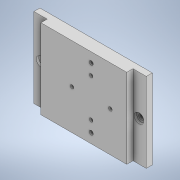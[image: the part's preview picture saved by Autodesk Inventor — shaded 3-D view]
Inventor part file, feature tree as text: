
AUTODESK INVENTOR PART (.ipt)
format: ipt  version: 2020 (Build 240168000, 168)  size: 148,480 bytes
history: native  units: in
note: dims shown in document units (in); Inventor stores cm internally (conversion verified against a paired STEP export)
features: sketch x5, hole x3, extrude x2
ambient origin geometry x8: Origin, YZ Plane, XZ Plane, XY Plane, X Axis, Y Axis, Z Axis, Center Point
bodies: Solid1 (feature_tree)
feature tree (10):
  extrude  "Extrusion1"  Depth=3.6654in
  extrude  "Extrusion2"  Depth=0.1969in TaperAngle=0.0deg
  hole  "Hole1"  [1 undecoded]
  hole  "Hole2"  [1 undecoded]
  hole  "Hole3"  [1 undecoded]
  sketch  "Sketch1"  dims[d2=0.4in d3=0.0in d4=3.6654in]
  sketch  "Sketch2"  dims[d5=2.5984in d6=0.1969in d7=0.0in]
  sketch  "Sketch3"  dims[d8=0.2362in d9=0.2362in]
  sketch  "Sketch4"  dims[d10=0.0in d11=0.0in]
  sketch  "Sketch5"  dims[d12=0.1772in d13=0.33in d14=0.315in d15=0.0787in d16=0.5635in d17=0.4843in d18=0.0in d19=0.9843in d20=1.9681in d21=1.1598in d22=1.1598in d23=0.1339in d24=0.33in d25=0.2559in d26=0.1181in d27=0.5635in d28=0.4843in d29=0.0in d32=0.2398in d33=0.0in d34=1.25in d35=0.116in d36=0.33in d37=0.2188in d38=0.112in d39=0.5635in d40=0.4843in d41=0.0in]
note: 3 required parameter values undecoded (feature->parameter linkage not recoverable at this tier; creation-order binding heuristic only, values carry confidence <= 0.55)
